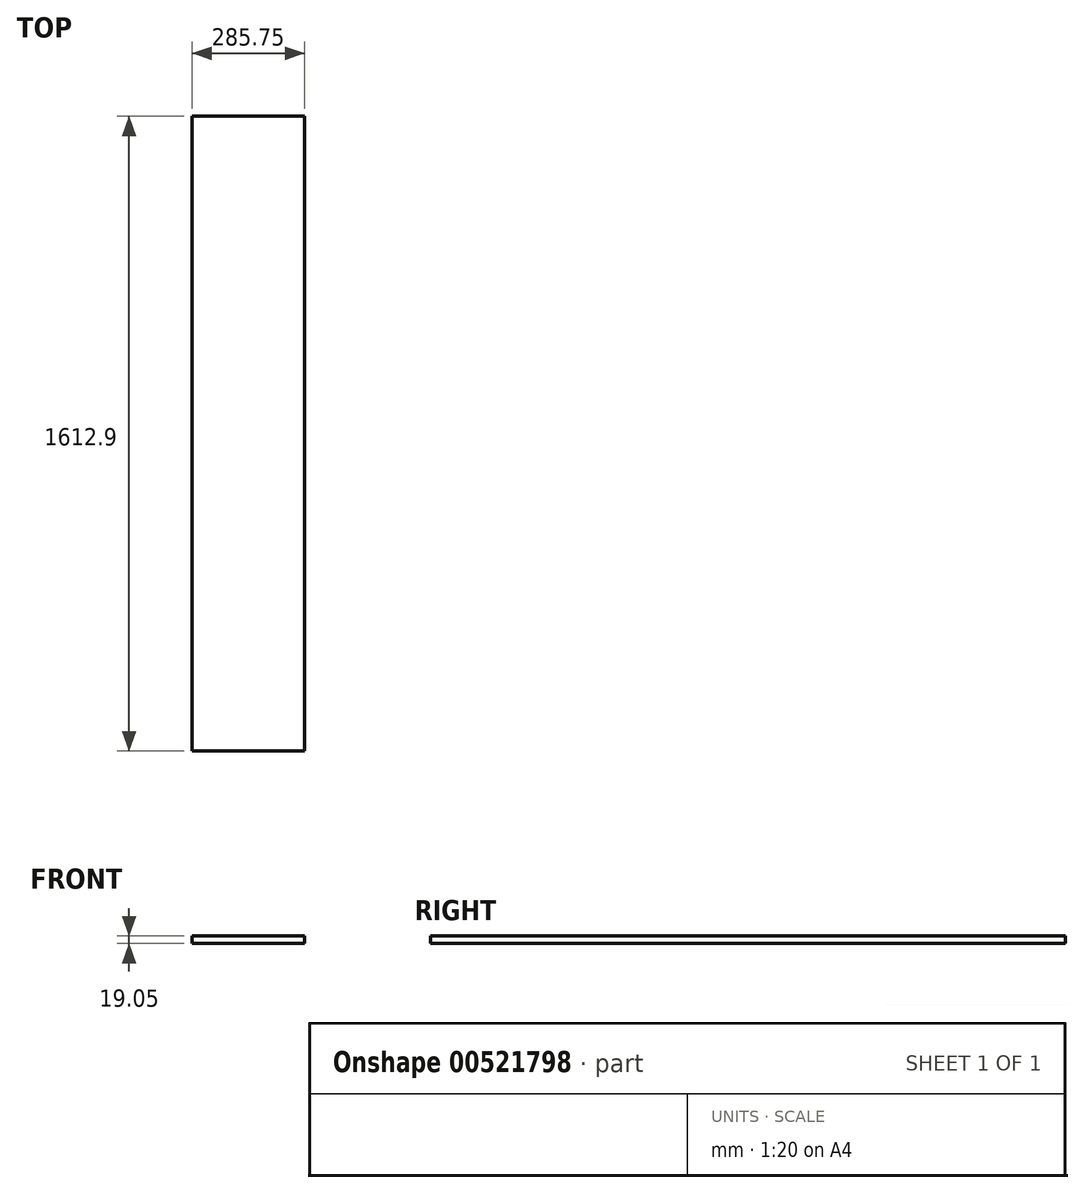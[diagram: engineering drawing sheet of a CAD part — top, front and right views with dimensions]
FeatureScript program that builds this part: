
annotation { "Feature Type Name" : "Feature", "Feature Type Description" : "" }
export const myFeature = defineFeature(function(context is Context, id is Id, definition is map)
    precondition{}
    {
        {
            var Q0;
            Q0=qCreatedBy(makeId("Front.planeOp"),FACE);
            var sketch = newSketch(context, id + "F0", { "sketchPlane" : qUnion([Q0])});
            skLineSegment(sketch, "E0.bottom", {"start": v(0, 0) * mm, "end": v(285.75, 0) * mm});
            skLineSegment(sketch, "E0.top", {"start": v(0, 19.05) * mm, "end": v(285.75, 19.05) * mm});
            skLineSegment(sketch, "E0.left", {"start": v(0, 0) * mm, "end": v(0, 19.05) * mm});
            skLineSegment(sketch, "E0.right", {"start": v(285.75, 0) * mm, "end": v(285.75, 19.05) * mm});
            skSolve(sketch);
        }
        {
            var Q0;
            Q0 = qSketchRegion(id + "F0", true);
            extrude(context, id + "F1", {"entities" : qUnion([Q0]), "oppositeDirection" : true, "depth" : 1612.9 * mm, "offsetDistance" : 25.4 * mm});
        }
    });
